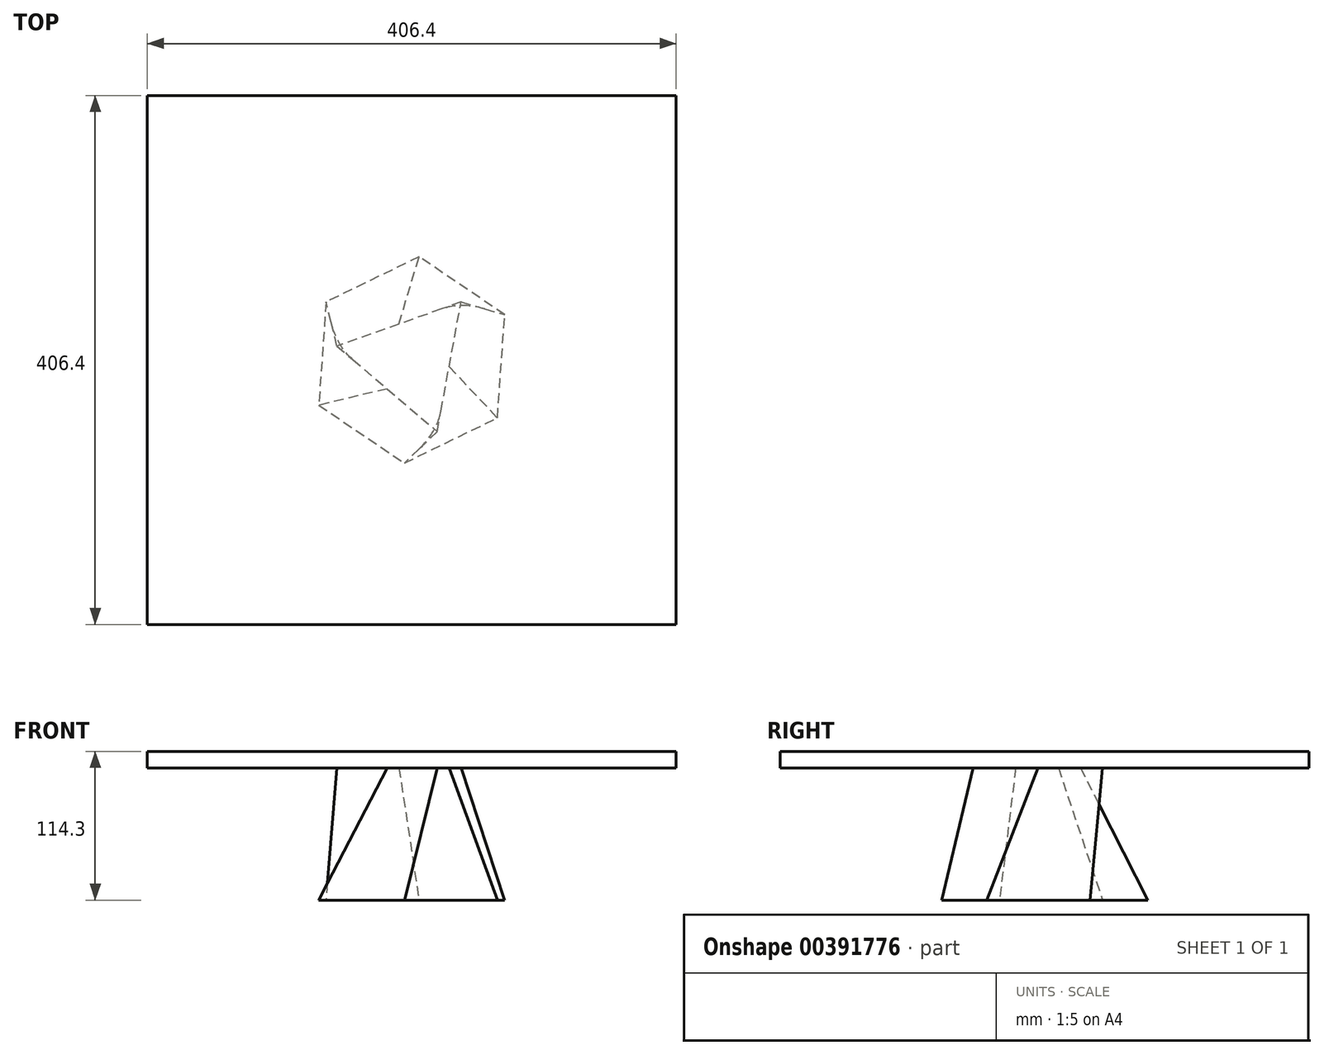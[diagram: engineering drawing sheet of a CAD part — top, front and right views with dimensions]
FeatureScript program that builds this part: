
annotation { "Feature Type Name" : "Feature", "Feature Type Description" : "" }
export const myFeature = defineFeature(function(context is Context, id is Id, definition is map)
    precondition{}
    {
        {
            var Q0;
            Q0=qCreatedBy(makeId("Top.planeOp"),FACE);
            var sketch = newSketch(context, id + "F0", { "sketchPlane" : qUnion([Q0])});
            skLineSegment(sketch, "E0.bottom", {"start": v(-203.2, 203.2) * mm, "end": v(203.2, 203.2) * mm});
            skLineSegment(sketch, "E0.top", {"start": v(-203.2, -203.2) * mm, "end": v(203.2, -203.2) * mm});
            skLineSegment(sketch, "E0.left", {"start": v(-203.2, 203.2) * mm, "end": v(-203.2, -203.2) * mm});
            skLineSegment(sketch, "E0.right", {"start": v(203.2, 203.2) * mm, "end": v(203.2, -203.2) * mm});
            skPoint(sketch, "E0.middle", {"position": v(0, 0) * mm});
            skSolve(sketch);
        }
        {
            var Q0;
            Q0=makeQuery(id+"F0.imprint","IMPRINT",FACE,{"disambiguationData":[TD([[makeQuery(id+"F0.imprint","IMPRINT",EDGE,{"derivedFrom":sQuery(id+"F0.wireOp",EDGE,"E0.bottom")}),-1.0]])]});
            extrude(context, id + "F1", {"entities" : qUnion([Q0]), "depth" : 12.7 * mm});
        }
        {
            var Q0;
            Q0=makeQuery(id+"F1.opExtrude","CAP_FACE",FACE,{"disambiguationData":[OSD([sQuery(id+"F0.wireOp",EDGE,"E0.bottom"),sQuery(id+"F0.wireOp",EDGE,"E0.top"),sQuery(id+"F0.wireOp",EDGE,"E0.left"),sQuery(id+"F0.wireOp",EDGE,"E0.right")])],"isStart":true});
            var sketch = newSketch(context, id + "F2", { "sketchPlane" : qUnion([Q0])});
            skCircle(sketch, "E1.cCircle", {"center": v(0, 0) * mm, "radius": 29.22 * mm, "construction": true});
            skLineSegment(sketch, "E1.0", {"start": v(-57.47, -10.57) * mm, "end": v(19.58, 55.06) * mm});
            skLineSegment(sketch, "E1.1", {"start": v(19.58, 55.06) * mm, "end": v(37.9, -44.48) * mm});
            skLineSegment(sketch, "E1.2", {"start": v(37.9, -44.48) * mm, "end": v(-57.47, -10.57) * mm});
            skPoint(sketch, "E1.0.midPoint", {"position": v(-18.95, 22.24) * mm});
            skSolve(sketch);
        }
        {
            var Q0;
            Q0=makeQuery(id+"F2.imprint","IMPRINT",FACE,{"disambiguationData":[TD([[makeQuery(id+"F2.imprint","IMPRINT",EDGE,{"derivedFrom":sQuery(id+"F2.wireOp",EDGE,"E1.0")}),1.0]])]});
            cPlane(context, id + "F3", {"entities" : qUnion([Q0]), "cplaneType" : CPlaneType.OFFSET, "offset" : 101.6 * mm, "width" : 152.4 * mm, "height" : 152.4 * mm});
        }
        {
            var Q0;
            Q0=qCreatedBy(id+"F3.planeOp",FACE);
            var sketch = newSketch(context, id + "F4", { "sketchPlane" : qUnion([Q0])});
            skCircle(sketch, "E2.cCircle", {"center": v(0, 0) * mm, "radius": 68.82 * mm, "construction": true});
            skLineSegment(sketch, "E2.0", {"start": v(-71.47, 34.75) * mm, "end": v(-5.64, 79.26) * mm});
            skLineSegment(sketch, "E2.1", {"start": v(-5.64, 79.26) * mm, "end": v(65.82, 44.52) * mm});
            skLineSegment(sketch, "E2.2", {"start": v(65.82, 44.52) * mm, "end": v(71.47, -34.75) * mm});
            skLineSegment(sketch, "E2.3", {"start": v(71.47, -34.75) * mm, "end": v(5.64, -79.26) * mm});
            skLineSegment(sketch, "E2.4", {"start": v(5.64, -79.26) * mm, "end": v(-65.82, -44.52) * mm});
            skLineSegment(sketch, "E2.5", {"start": v(-65.82, -44.52) * mm, "end": v(-71.47, 34.75) * mm});
            skPoint(sketch, "E2.0.midPoint", {"position": v(-38.55, 57) * mm});
            skSolve(sketch);
        }
        {
            var Q1;
            Q1=makeQuery(id+"F2.imprint","IMPRINT",FACE,{"disambiguationData":[TD([[makeQuery(id+"F2.imprint","IMPRINT",EDGE,{"derivedFrom":sQuery(id+"F2.wireOp",EDGE,"E1.0")}),-1.0]])]});
            var Q2;
            Q2=makeQuery(id+"F4.imprint","IMPRINT",FACE,{"disambiguationData":[TD([[makeQuery(id+"F4.imprint","IMPRINT",EDGE,{"derivedFrom":sQuery(id+"F4.wireOp",EDGE,"E2.0")}),-1.0]])]});
            loft(context, id + "F5", {"operationType" : NewBodyOperationType.ADD, "sheetProfilesArray" : [{ "sheetProfileEntities" : qUnion([Q1]) }, { "sheetProfileEntities" : qUnion([Q2]) }]});
        }
    });
